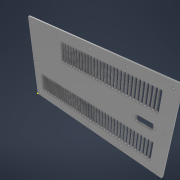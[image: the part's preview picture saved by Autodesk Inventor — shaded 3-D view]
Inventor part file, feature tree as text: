
AUTODESK INVENTOR PART (.ipt)
format: ipt  version: 2022 (Build 260153000, 153)  size: 2,114,560 bytes
history: native  units: mm
features: other x2, sketch x2, extrude x1
ambient origin geometry x8: Origin, YZ Plane, XZ Plane, XY Plane, X Axis, Y Axis, Z Axis, Center Point
bodies: Body1 (feature_tree)
feature tree (5):
  other  "РабПлоскость5"
  sketch  "Эскиз1"
  extrude  "Выдавливание2"  Depth=156.0mm
  sketch  "Эскиз2"
  other  "Картинка3"
